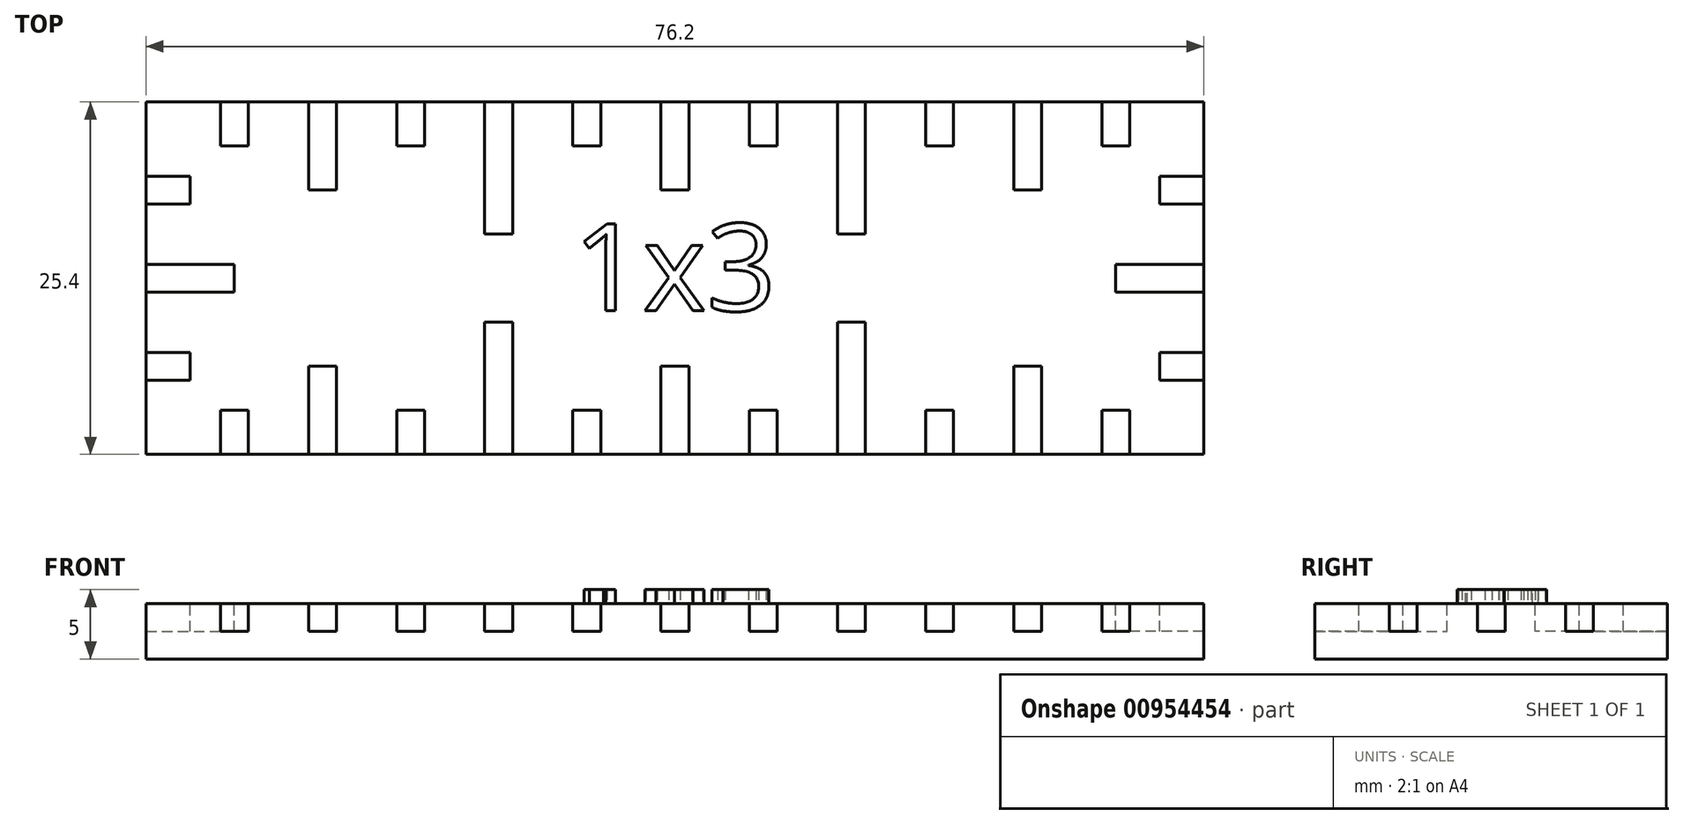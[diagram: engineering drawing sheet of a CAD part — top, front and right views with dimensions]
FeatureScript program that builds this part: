
annotation { "Feature Type Name" : "Feature", "Feature Type Description" : "" }
export const myFeature = defineFeature(function(context is Context, id is Id, definition is map)
    precondition{}
    {
        {
            var Q0;
            Q0=qCreatedBy(makeId("Top.planeOp"),FACE);
            var sketch = newSketch(context, id + "F0", { "sketchPlane" : qUnion([Q0])});
            skLineSegment(sketch, "E0.bottom", {"start": v(-38.1, 12.7) * mm, "end": v(38.1, 12.7) * mm});
            skLineSegment(sketch, "E0.top", {"start": v(-38.1, -12.7) * mm, "end": v(38.1, -12.7) * mm});
            skLineSegment(sketch, "E0.left", {"start": v(-38.1, 12.7) * mm, "end": v(-38.1, -12.7) * mm});
            skLineSegment(sketch, "E0.right", {"start": v(38.1, 12.7) * mm, "end": v(38.1, -12.7) * mm});
            skPoint(sketch, "E0.middle", {"position": v(0, 0) * mm});
            skSolve(sketch);
        }
        {
            var Q0;
            Q0=makeQuery(id+"F0.imprint","IMPRINT",FACE,{"disambiguationData":[TD([[makeQuery(id+"F0.imprint","IMPRINT",EDGE,{"derivedFrom":sQuery(id+"F0.wireOp",EDGE,"E0.bottom")}),-1.0]])]});
            extrude(context, id + "F1", {"entities" : qUnion([Q0]), "depth" : 4 * mm, "offsetDistance" : 25 * mm});
        }
        {
            var Q0;
            Q0=makeQuery(id+"F1.opExtrude","CAP_FACE",FACE,{"disambiguationData":[OSD([sQuery(id+"F0.wireOp",EDGE,"E0.bottom"),sQuery(id+"F0.wireOp",EDGE,"E0.top"),sQuery(id+"F0.wireOp",EDGE,"E0.left"),sQuery(id+"F0.wireOp",EDGE,"E0.right")])],"isStart":false});
            var sketch = newSketch(context, id + "F2", { "sketchPlane" : qUnion([Q0])});
            skLineSegment(sketch, "E1.bottom", {"start": v(-1, -6.35) * mm, "end": v(1, -6.35) * mm});
            skLineSegment(sketch, "E1.top", {"start": v(-1, -19.05) * mm, "end": v(1, -19.05) * mm});
            skLineSegment(sketch, "E1.left", {"start": v(-1, -6.35) * mm, "end": v(-1, -19.05) * mm});
            skLineSegment(sketch, "E1.right", {"start": v(1, -6.35) * mm, "end": v(1, -19.05) * mm});
            skPoint(sketch, "E1.middle", {"position": v(0, -12.7) * mm});
            skLineSegment(sketch, "E2.bottom", {"start": v(5.35, -9.53) * mm, "end": v(7.35, -9.53) * mm});
            skLineSegment(sketch, "E2.top", {"start": v(5.35, -15.88) * mm, "end": v(7.35, -15.88) * mm});
            skLineSegment(sketch, "E2.left", {"start": v(5.35, -9.53) * mm, "end": v(5.35, -15.88) * mm});
            skLineSegment(sketch, "E2.right", {"start": v(7.35, -9.53) * mm, "end": v(7.35, -15.88) * mm});
            skPoint(sketch, "E2.middle", {"position": v(6.35, -12.7) * mm});
            skLineSegment(sketch, "E3.bottom", {"start": v(-7.35, -9.53) * mm, "end": v(-5.35, -9.53) * mm});
            skLineSegment(sketch, "E3.top", {"start": v(-7.35, -15.88) * mm, "end": v(-5.35, -15.88) * mm});
            skLineSegment(sketch, "E3.left", {"start": v(-7.35, -9.53) * mm, "end": v(-7.35, -15.88) * mm});
            skLineSegment(sketch, "E3.right", {"start": v(-5.35, -9.53) * mm, "end": v(-5.35, -15.88) * mm});
            skPoint(sketch, "E3.middle", {"position": v(-6.35, -12.7) * mm});
            skLineSegment(sketch, "E4.bottom", {"start": v(-44.45, -1) * mm, "end": v(-44.45, 1) * mm});
            skLineSegment(sketch, "E4.top", {"start": v(-31.75, -1) * mm, "end": v(-31.75, 1) * mm});
            skLineSegment(sketch, "E4.left", {"start": v(-44.45, -1) * mm, "end": v(-31.75, -1) * mm});
            skLineSegment(sketch, "E4.right", {"start": v(-44.45, 1) * mm, "end": v(-31.75, 1) * mm});
            skPoint(sketch, "E4.middle", {"position": v(-38.1, 0) * mm});
            skLineSegment(sketch, "E5.bottom", {"start": v(-41.27, 5.35) * mm, "end": v(-41.27, 7.35) * mm});
            skLineSegment(sketch, "E5.top", {"start": v(-34.92, 5.35) * mm, "end": v(-34.92, 7.35) * mm});
            skLineSegment(sketch, "E5.left", {"start": v(-41.27, 5.35) * mm, "end": v(-34.92, 5.35) * mm});
            skLineSegment(sketch, "E5.right", {"start": v(-41.27, 7.35) * mm, "end": v(-34.92, 7.35) * mm});
            skPoint(sketch, "E5.middle", {"position": v(-38.1, 6.35) * mm});
            skLineSegment(sketch, "E6.bottom", {"start": v(-41.27, -7.35) * mm, "end": v(-41.27, -5.35) * mm});
            skLineSegment(sketch, "E6.top", {"start": v(-34.92, -7.35) * mm, "end": v(-34.92, -5.35) * mm});
            skLineSegment(sketch, "E6.left", {"start": v(-41.27, -7.35) * mm, "end": v(-34.92, -7.35) * mm});
            skLineSegment(sketch, "E6.right", {"start": v(-41.27, -5.35) * mm, "end": v(-34.92, -5.35) * mm});
            skPoint(sketch, "E6.middle", {"position": v(-38.1, -6.35) * mm});
            skLineSegment(sketch, "E7.bottom", {"start": v(1, 6.35) * mm, "end": v(-1, 6.35) * mm});
            skLineSegment(sketch, "E7.top", {"start": v(1, 19.05) * mm, "end": v(-1, 19.05) * mm});
            skLineSegment(sketch, "E7.left", {"start": v(1, 6.35) * mm, "end": v(1, 19.05) * mm});
            skLineSegment(sketch, "E7.right", {"start": v(-1, 6.35) * mm, "end": v(-1, 19.05) * mm});
            skPoint(sketch, "E7.middle", {"position": v(0, 12.7) * mm});
            skLineSegment(sketch, "E8.bottom", {"start": v(-5.35, 9.53) * mm, "end": v(-7.35, 9.53) * mm});
            skLineSegment(sketch, "E8.top", {"start": v(-5.35, 15.88) * mm, "end": v(-7.35, 15.88) * mm});
            skLineSegment(sketch, "E8.left", {"start": v(-5.35, 9.53) * mm, "end": v(-5.35, 15.88) * mm});
            skLineSegment(sketch, "E8.right", {"start": v(-7.35, 9.53) * mm, "end": v(-7.35, 15.88) * mm});
            skPoint(sketch, "E8.middle", {"position": v(-6.35, 12.7) * mm});
            skLineSegment(sketch, "E9.bottom", {"start": v(7.35, 9.52) * mm, "end": v(5.35, 9.52) * mm});
            skLineSegment(sketch, "E9.top", {"start": v(7.35, 15.88) * mm, "end": v(5.35, 15.88) * mm});
            skLineSegment(sketch, "E9.left", {"start": v(7.35, 9.52) * mm, "end": v(7.35, 15.88) * mm});
            skLineSegment(sketch, "E9.right", {"start": v(5.35, 9.52) * mm, "end": v(5.35, 15.88) * mm});
            skPoint(sketch, "E9.middle", {"position": v(6.35, 12.7) * mm});
            skLineSegment(sketch, "E10.bottom", {"start": v(44.45, 1) * mm, "end": v(44.45, -1) * mm});
            skLineSegment(sketch, "E10.top", {"start": v(31.75, 1) * mm, "end": v(31.75, -1) * mm});
            skLineSegment(sketch, "E10.left", {"start": v(44.45, 1) * mm, "end": v(31.75, 1) * mm});
            skLineSegment(sketch, "E10.right", {"start": v(44.45, -1) * mm, "end": v(31.75, -1) * mm});
            skPoint(sketch, "E10.middle", {"position": v(38.1, 0) * mm});
            skLineSegment(sketch, "E11.bottom", {"start": v(41.28, -5.35) * mm, "end": v(41.28, -7.35) * mm});
            skLineSegment(sketch, "E11.top", {"start": v(34.93, -5.35) * mm, "end": v(34.93, -7.35) * mm});
            skLineSegment(sketch, "E11.left", {"start": v(41.28, -5.35) * mm, "end": v(34.93, -5.35) * mm});
            skLineSegment(sketch, "E11.right", {"start": v(41.28, -7.35) * mm, "end": v(34.93, -7.35) * mm});
            skPoint(sketch, "E11.middle", {"position": v(38.1, -6.35) * mm});
            skLineSegment(sketch, "E12.bottom", {"start": v(41.28, 7.35) * mm, "end": v(41.28, 5.35) * mm});
            skLineSegment(sketch, "E12.top", {"start": v(34.93, 7.35) * mm, "end": v(34.93, 5.35) * mm});
            skLineSegment(sketch, "E12.left", {"start": v(41.28, 7.35) * mm, "end": v(34.93, 7.35) * mm});
            skLineSegment(sketch, "E12.right", {"start": v(41.28, 5.35) * mm, "end": v(34.93, 5.35) * mm});
            skPoint(sketch, "E12.middle", {"position": v(38.1, 6.35) * mm});
            skLineSegment(sketch, "E13.bottom", {"start": v(-11.7, 3.18) * mm, "end": v(-13.7, 3.18) * mm});
            skLineSegment(sketch, "E13.top", {"start": v(-11.7, 22.23) * mm, "end": v(-13.7, 22.23) * mm});
            skLineSegment(sketch, "E13.left", {"start": v(-11.7, 3.18) * mm, "end": v(-11.7, 22.23) * mm});
            skLineSegment(sketch, "E13.right", {"start": v(-13.7, 3.18) * mm, "end": v(-13.7, 22.23) * mm});
            skPoint(sketch, "E13.middle", {"position": v(-12.7, 12.7) * mm});
            skLineSegment(sketch, "E14.bottom", {"start": v(-18.05, 9.53) * mm, "end": v(-20.05, 9.53) * mm});
            skLineSegment(sketch, "E14.top", {"start": v(-18.05, 15.88) * mm, "end": v(-20.05, 15.88) * mm});
            skLineSegment(sketch, "E14.left", {"start": v(-18.05, 9.53) * mm, "end": v(-18.05, 15.88) * mm});
            skLineSegment(sketch, "E14.right", {"start": v(-20.05, 9.53) * mm, "end": v(-20.05, 15.88) * mm});
            skPoint(sketch, "E14.middle", {"position": v(-19.05, 12.7) * mm});
            skLineSegment(sketch, "E15.bottom", {"start": v(-11.7, -22.23) * mm, "end": v(-13.7, -22.23) * mm});
            skLineSegment(sketch, "E15.top", {"start": v(-11.7, -3.18) * mm, "end": v(-13.7, -3.18) * mm});
            skLineSegment(sketch, "E15.left", {"start": v(-11.7, -22.23) * mm, "end": v(-11.7, -3.18) * mm});
            skLineSegment(sketch, "E15.right", {"start": v(-13.7, -22.23) * mm, "end": v(-13.7, -3.18) * mm});
            skPoint(sketch, "E15.middle", {"position": v(-12.7, -12.7) * mm});
            skLineSegment(sketch, "E16.bottom", {"start": v(-18.05, -15.88) * mm, "end": v(-20.05, -15.88) * mm});
            skLineSegment(sketch, "E16.top", {"start": v(-18.05, -9.53) * mm, "end": v(-20.05, -9.53) * mm});
            skLineSegment(sketch, "E16.left", {"start": v(-18.05, -15.88) * mm, "end": v(-18.05, -9.53) * mm});
            skLineSegment(sketch, "E16.right", {"start": v(-20.05, -15.88) * mm, "end": v(-20.05, -9.53) * mm});
            skPoint(sketch, "E16.middle", {"position": v(-19.05, -12.7) * mm});
            skLineSegment(sketch, "E17.bottom", {"start": v(-5.35, -15.88) * mm, "end": v(-7.35, -15.88) * mm});
            skLineSegment(sketch, "E17.top", {"start": v(-5.35, -9.53) * mm, "end": v(-7.35, -9.53) * mm});
            skLineSegment(sketch, "E17.left", {"start": v(-5.35, -15.88) * mm, "end": v(-5.35, -9.53) * mm});
            skLineSegment(sketch, "E17.right", {"start": v(-7.35, -15.88) * mm, "end": v(-7.35, -9.53) * mm});
            skLineSegment(sketch, "E18.bottom", {"start": v(11.7, -3.18) * mm, "end": v(13.7, -3.18) * mm});
            skLineSegment(sketch, "E18.top", {"start": v(11.7, -22.23) * mm, "end": v(13.7, -22.23) * mm});
            skLineSegment(sketch, "E18.left", {"start": v(11.7, -3.18) * mm, "end": v(11.7, -22.23) * mm});
            skLineSegment(sketch, "E18.right", {"start": v(13.7, -3.18) * mm, "end": v(13.7, -22.23) * mm});
            skPoint(sketch, "E18.middle", {"position": v(12.7, -12.7) * mm});
            skLineSegment(sketch, "E19.bottom", {"start": v(18.05, -9.53) * mm, "end": v(20.05, -9.53) * mm});
            skLineSegment(sketch, "E19.top", {"start": v(18.05, -15.88) * mm, "end": v(20.05, -15.88) * mm});
            skLineSegment(sketch, "E19.left", {"start": v(18.05, -9.53) * mm, "end": v(18.05, -15.88) * mm});
            skLineSegment(sketch, "E19.right", {"start": v(20.05, -9.53) * mm, "end": v(20.05, -15.88) * mm});
            skPoint(sketch, "E19.middle", {"position": v(19.05, -12.7) * mm});
            skLineSegment(sketch, "E20.bottom", {"start": v(11.7, 22.23) * mm, "end": v(13.7, 22.23) * mm});
            skLineSegment(sketch, "E20.top", {"start": v(11.7, 3.18) * mm, "end": v(13.7, 3.18) * mm});
            skLineSegment(sketch, "E20.left", {"start": v(11.7, 22.23) * mm, "end": v(11.7, 3.18) * mm});
            skLineSegment(sketch, "E20.right", {"start": v(13.7, 22.23) * mm, "end": v(13.7, 3.18) * mm});
            skPoint(sketch, "E20.middle", {"position": v(12.7, 12.7) * mm});
            skLineSegment(sketch, "E21.bottom", {"start": v(18.05, 15.88) * mm, "end": v(20.05, 15.88) * mm});
            skLineSegment(sketch, "E21.top", {"start": v(18.05, 9.53) * mm, "end": v(20.05, 9.53) * mm});
            skLineSegment(sketch, "E21.left", {"start": v(18.05, 15.88) * mm, "end": v(18.05, 9.53) * mm});
            skLineSegment(sketch, "E21.right", {"start": v(20.05, 15.88) * mm, "end": v(20.05, 9.53) * mm});
            skPoint(sketch, "E21.middle", {"position": v(19.05, 12.7) * mm});
            skLineSegment(sketch, "E22.bottom", {"start": v(5.35, 15.88) * mm, "end": v(7.35, 15.88) * mm});
            skLineSegment(sketch, "E22.top", {"start": v(5.35, 9.53) * mm, "end": v(7.35, 9.53) * mm});
            skLineSegment(sketch, "E22.left", {"start": v(5.35, 15.88) * mm, "end": v(5.35, 9.53) * mm});
            skLineSegment(sketch, "E22.right", {"start": v(7.35, 15.88) * mm, "end": v(7.35, 9.53) * mm});
            skLineSegment(sketch, "E23.bottom", {"start": v(26.4, 6.35) * mm, "end": v(24.4, 6.35) * mm});
            skLineSegment(sketch, "E23.top", {"start": v(26.4, 19.05) * mm, "end": v(24.4, 19.05) * mm});
            skLineSegment(sketch, "E23.left", {"start": v(26.4, 6.35) * mm, "end": v(26.4, 19.05) * mm});
            skLineSegment(sketch, "E23.right", {"start": v(24.4, 6.35) * mm, "end": v(24.4, 19.05) * mm});
            skPoint(sketch, "E23.middle", {"position": v(25.4, 12.7) * mm});
            skLineSegment(sketch, "E24.bottom", {"start": v(20.05, 9.53) * mm, "end": v(18.05, 9.53) * mm});
            skLineSegment(sketch, "E24.top", {"start": v(20.05, 15.88) * mm, "end": v(18.05, 15.88) * mm});
            skLineSegment(sketch, "E24.left", {"start": v(20.05, 9.53) * mm, "end": v(20.05, 15.88) * mm});
            skLineSegment(sketch, "E24.right", {"start": v(18.05, 9.53) * mm, "end": v(18.05, 15.88) * mm});
            skLineSegment(sketch, "E25.bottom", {"start": v(32.75, 9.52) * mm, "end": v(30.75, 9.52) * mm});
            skLineSegment(sketch, "E25.top", {"start": v(32.75, 15.88) * mm, "end": v(30.75, 15.88) * mm});
            skLineSegment(sketch, "E25.left", {"start": v(32.75, 9.52) * mm, "end": v(32.75, 15.88) * mm});
            skLineSegment(sketch, "E25.right", {"start": v(30.75, 9.52) * mm, "end": v(30.75, 15.88) * mm});
            skPoint(sketch, "E25.middle", {"position": v(31.75, 12.7) * mm});
            skLineSegment(sketch, "E26.bottom", {"start": v(30.75, 15.88) * mm, "end": v(32.75, 15.88) * mm});
            skLineSegment(sketch, "E26.top", {"start": v(30.75, 9.53) * mm, "end": v(32.75, 9.53) * mm});
            skLineSegment(sketch, "E26.left", {"start": v(30.75, 15.88) * mm, "end": v(30.75, 9.53) * mm});
            skLineSegment(sketch, "E26.right", {"start": v(32.75, 15.88) * mm, "end": v(32.75, 9.53) * mm});
            skLineSegment(sketch, "E27.bottom", {"start": v(26.4, -19.05) * mm, "end": v(24.4, -19.05) * mm});
            skLineSegment(sketch, "E27.top", {"start": v(26.4, -6.35) * mm, "end": v(24.4, -6.35) * mm});
            skLineSegment(sketch, "E27.left", {"start": v(26.4, -19.05) * mm, "end": v(26.4, -6.35) * mm});
            skLineSegment(sketch, "E27.right", {"start": v(24.4, -19.05) * mm, "end": v(24.4, -6.35) * mm});
            skPoint(sketch, "E27.middle", {"position": v(25.4, -12.7) * mm});
            skLineSegment(sketch, "E28.bottom", {"start": v(20.05, -15.88) * mm, "end": v(18.05, -15.88) * mm});
            skLineSegment(sketch, "E28.top", {"start": v(20.05, -9.53) * mm, "end": v(18.05, -9.53) * mm});
            skLineSegment(sketch, "E28.left", {"start": v(20.05, -15.88) * mm, "end": v(20.05, -9.52) * mm});
            skLineSegment(sketch, "E28.right", {"start": v(18.05, -15.88) * mm, "end": v(18.05, -9.52) * mm});
            skLineSegment(sketch, "E29.bottom", {"start": v(32.75, -15.88) * mm, "end": v(30.75, -15.88) * mm});
            skLineSegment(sketch, "E29.top", {"start": v(32.75, -9.53) * mm, "end": v(30.75, -9.53) * mm});
            skLineSegment(sketch, "E29.left", {"start": v(32.75, -15.88) * mm, "end": v(32.75, -9.52) * mm});
            skLineSegment(sketch, "E29.right", {"start": v(30.75, -15.88) * mm, "end": v(30.75, -9.52) * mm});
            skPoint(sketch, "E29.middle", {"position": v(31.75, -12.7) * mm});
            skLineSegment(sketch, "E30.bottom", {"start": v(20.05, -15.87) * mm, "end": v(18.05, -15.87) * mm});
            skLineSegment(sketch, "E30.top", {"start": v(20.05, -9.52) * mm, "end": v(18.05, -9.52) * mm});
            skLineSegment(sketch, "E30.left", {"start": v(20.05, -15.87) * mm, "end": v(20.05, -9.52) * mm});
            skLineSegment(sketch, "E30.right", {"start": v(18.05, -15.87) * mm, "end": v(18.05, -9.52) * mm});
            skLineSegment(sketch, "E31.bottom", {"start": v(30.75, -9.52) * mm, "end": v(32.75, -9.52) * mm});
            skLineSegment(sketch, "E31.top", {"start": v(30.75, -15.88) * mm, "end": v(32.75, -15.88) * mm});
            skLineSegment(sketch, "E31.left", {"start": v(30.75, -9.52) * mm, "end": v(30.75, -15.88) * mm});
            skLineSegment(sketch, "E31.right", {"start": v(32.75, -9.52) * mm, "end": v(32.75, -15.88) * mm});
            skLineSegment(sketch, "E32.bottom", {"start": v(-26.4, -6.35) * mm, "end": v(-24.4, -6.35) * mm});
            skLineSegment(sketch, "E32.top", {"start": v(-26.4, -19.05) * mm, "end": v(-24.4, -19.05) * mm});
            skLineSegment(sketch, "E32.left", {"start": v(-26.4, -6.35) * mm, "end": v(-26.4, -19.05) * mm});
            skLineSegment(sketch, "E32.right", {"start": v(-24.4, -6.35) * mm, "end": v(-24.4, -19.05) * mm});
            skPoint(sketch, "E32.middle", {"position": v(-25.4, -12.7) * mm});
            skLineSegment(sketch, "E33.bottom", {"start": v(-20.05, -9.53) * mm, "end": v(-18.05, -9.53) * mm});
            skLineSegment(sketch, "E33.top", {"start": v(-20.05, -15.88) * mm, "end": v(-18.05, -15.88) * mm});
            skLineSegment(sketch, "E33.left", {"start": v(-20.05, -9.53) * mm, "end": v(-20.05, -15.88) * mm});
            skLineSegment(sketch, "E33.right", {"start": v(-18.05, -9.53) * mm, "end": v(-18.05, -15.88) * mm});
            skLineSegment(sketch, "E34.bottom", {"start": v(-32.75, -9.53) * mm, "end": v(-30.75, -9.53) * mm});
            skLineSegment(sketch, "E34.top", {"start": v(-32.75, -15.88) * mm, "end": v(-30.75, -15.88) * mm});
            skLineSegment(sketch, "E34.left", {"start": v(-32.75, -9.53) * mm, "end": v(-32.75, -15.88) * mm});
            skLineSegment(sketch, "E34.right", {"start": v(-30.75, -9.53) * mm, "end": v(-30.75, -15.88) * mm});
            skPoint(sketch, "E34.middle", {"position": v(-31.75, -12.7) * mm});
            skLineSegment(sketch, "E35.bottom", {"start": v(-30.75, -15.88) * mm, "end": v(-32.75, -15.88) * mm});
            skLineSegment(sketch, "E35.top", {"start": v(-30.75, -9.53) * mm, "end": v(-32.75, -9.53) * mm});
            skLineSegment(sketch, "E35.left", {"start": v(-30.75, -15.88) * mm, "end": v(-30.75, -9.53) * mm});
            skLineSegment(sketch, "E35.right", {"start": v(-32.75, -15.88) * mm, "end": v(-32.75, -9.53) * mm});
            skLineSegment(sketch, "E36.bottom", {"start": v(-26.4, 19.05) * mm, "end": v(-24.4, 19.05) * mm});
            skLineSegment(sketch, "E36.top", {"start": v(-26.4, 6.35) * mm, "end": v(-24.4, 6.35) * mm});
            skLineSegment(sketch, "E36.left", {"start": v(-26.4, 19.05) * mm, "end": v(-26.4, 6.35) * mm});
            skLineSegment(sketch, "E36.right", {"start": v(-24.4, 19.05) * mm, "end": v(-24.4, 6.35) * mm});
            skPoint(sketch, "E36.middle", {"position": v(-25.4, 12.7) * mm});
            skLineSegment(sketch, "E37.bottom", {"start": v(-20.05, 15.88) * mm, "end": v(-18.05, 15.88) * mm});
            skLineSegment(sketch, "E37.top", {"start": v(-20.05, 9.53) * mm, "end": v(-18.05, 9.53) * mm});
            skLineSegment(sketch, "E37.left", {"start": v(-20.05, 15.88) * mm, "end": v(-20.05, 9.53) * mm});
            skLineSegment(sketch, "E37.right", {"start": v(-18.05, 15.88) * mm, "end": v(-18.05, 9.53) * mm});
            skLineSegment(sketch, "E38.bottom", {"start": v(-32.75, 15.88) * mm, "end": v(-30.75, 15.88) * mm});
            skLineSegment(sketch, "E38.top", {"start": v(-32.75, 9.53) * mm, "end": v(-30.75, 9.53) * mm});
            skLineSegment(sketch, "E38.left", {"start": v(-32.75, 15.88) * mm, "end": v(-32.75, 9.53) * mm});
            skLineSegment(sketch, "E38.right", {"start": v(-30.75, 15.88) * mm, "end": v(-30.75, 9.53) * mm});
            skPoint(sketch, "E38.middle", {"position": v(-31.75, 12.7) * mm});
            skLineSegment(sketch, "E39.bottom", {"start": v(-30.75, 9.53) * mm, "end": v(-32.75, 9.53) * mm});
            skLineSegment(sketch, "E39.top", {"start": v(-30.75, 15.88) * mm, "end": v(-32.75, 15.88) * mm});
            skLineSegment(sketch, "E39.left", {"start": v(-30.75, 9.53) * mm, "end": v(-30.75, 15.88) * mm});
            skLineSegment(sketch, "E39.right", {"start": v(-32.75, 9.53) * mm, "end": v(-32.75, 15.88) * mm});
            skSolve(sketch);
        }
        {
            var Q0;
            Q0=qSketchRegion(id+"F2",true);
            extrude(context, id + "F3", {"entities" : qUnion([Q0]), "operationType" : NewBodyOperationType.REMOVE, "oppositeDirection" : true, "depth" : 2 * mm, "offsetDistance" : 25 * mm});
        }
        {
            var Q0;
            Q0=makeQuery(id+"F1.opExtrude","CAP_FACE",FACE,{"disambiguationData":[OSD([sQuery(id+"F0.wireOp",EDGE,"E0.bottom"),sQuery(id+"F0.wireOp",EDGE,"E0.top"),sQuery(id+"F0.wireOp",EDGE,"E0.left"),sQuery(id+"F0.wireOp",EDGE,"E0.right")])],"isStart":false});
            var sketch = newSketch(context, id + "F4", { "sketchPlane" : qUnion([Q0])});
            skText(sketch, "E40", { "text": "1x3", "fontName": "OpenSans-Regular.ttf"});
            const initialGuessF4  = {"E40": [-0.00735, -0.00235, 1, 0, 0.00632]};
            skSetInitialGuess(sketch, initialGuessF4);
            skSolve(sketch);
        }
        {
            var Q0;
            Q0=qSketchRegion(id+"F4",true);
            extrude(context, id + "F5", {"entities" : qUnion([Q0]), "operationType" : NewBodyOperationType.ADD, "depth" : 1 * mm, "offsetDistance" : 25 * mm});
        }
    });
